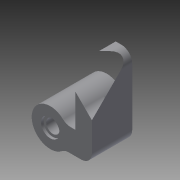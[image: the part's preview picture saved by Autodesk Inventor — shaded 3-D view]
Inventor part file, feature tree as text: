
AUTODESK INVENTOR PART (.ipt)
format: ipt  version: 2015 (Build 190159000, 159)  size: 137,728 bytes
history: native  units: in
note: dims shown in document units (in); Inventor stores cm internally (conversion verified against a paired STEP export)
features: extrude x4, sketch x4, mirror x2, fillet x1, reference x1
ambient origin geometry x8: Origin, YZ Plane, XZ Plane, XY Plane, X Axis, Y Axis, Z Axis, Center Point
bodies: Solid1 (feature_tree)
feature tree (12):
  extrude  "Extrusion1"  Depth=0.9375in TaperAngle=0.0deg
  extrude  "Extrusion2"  Depth=0.4882in TaperAngle=0.0deg
  mirror  "Mirror1"
  extrude  "Extrusion3"  Depth=0.0591in TaperAngle=0.0deg
  extrude  "Extrusion4"  Depth=1.8455in
  fillet  "Fillet1"  [1 undecoded]
  mirror  "Mirror2"
  sketch  "Sketch1"  dims[d0=0.375in d1=0.0in d2=0.9375in d3=0.0in]
  reference  "Reference1"
  sketch  "Sketch2"  dims[d4=0.3125in d5=0.4882in d6=0.0in]
  sketch  "Sketch3"  dims[d7=0.4331in d8=0.0591in d9=0.0in]
  sketch  "Sketch4"  dims[d10=0.25in d11=1.8455in]
note: 1 required parameter value undecoded (feature->parameter linkage not recoverable at this tier; creation-order binding heuristic only, values carry confidence <= 0.55)
